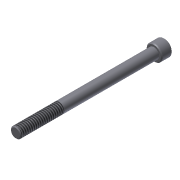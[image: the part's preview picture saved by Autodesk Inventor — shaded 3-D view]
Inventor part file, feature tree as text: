
AUTODESK INVENTOR PART (.ipt)
format: ipt  version: 2013 (Build 170138000, 138)  size: 99,328 bytes
history: native  units: in
note: dims shown in document units (in); Inventor stores cm internally (conversion verified against a paired STEP export)
features: extrude x3, sketch x3, chamfer x1, thread x1
ambient origin geometry x8: Origin, YZ Plane, XZ Plane, XY Plane, X Axis, Y Axis, Z Axis, Center Point
bodies: Solid1 (feature_tree)
feature tree (8):
  extrude  "Extrusion1"  Depth=3.25in TaperAngle=0.0deg
  extrude  "Extrusion2"  Depth=0.25in TaperAngle=0.0deg
  extrude  "Extrusion3"  Depth=0.125in TaperAngle=0.0deg
  chamfer  "Chamfer1"  Distance=0.02in Angle=45.0deg
  thread  "Thread1"  [1 undecoded]
  sketch  "Sketch1"  dims[d0=0.25in d1=3.25in d2=0.0in]
  sketch  "Sketch2"  dims[d3=0.375in d4=0.25in d5=0.0in]
  sketch  "Sketch3"  dims[d6=0.1875in d7=0.125in d8=0.0in d9=0.02in d10=0.125in d11=45.0deg d12=1.0in d13=0.0in]
note: 1 required parameter value undecoded (feature->parameter linkage not recoverable at this tier; creation-order binding heuristic only, values carry confidence <= 0.55)
